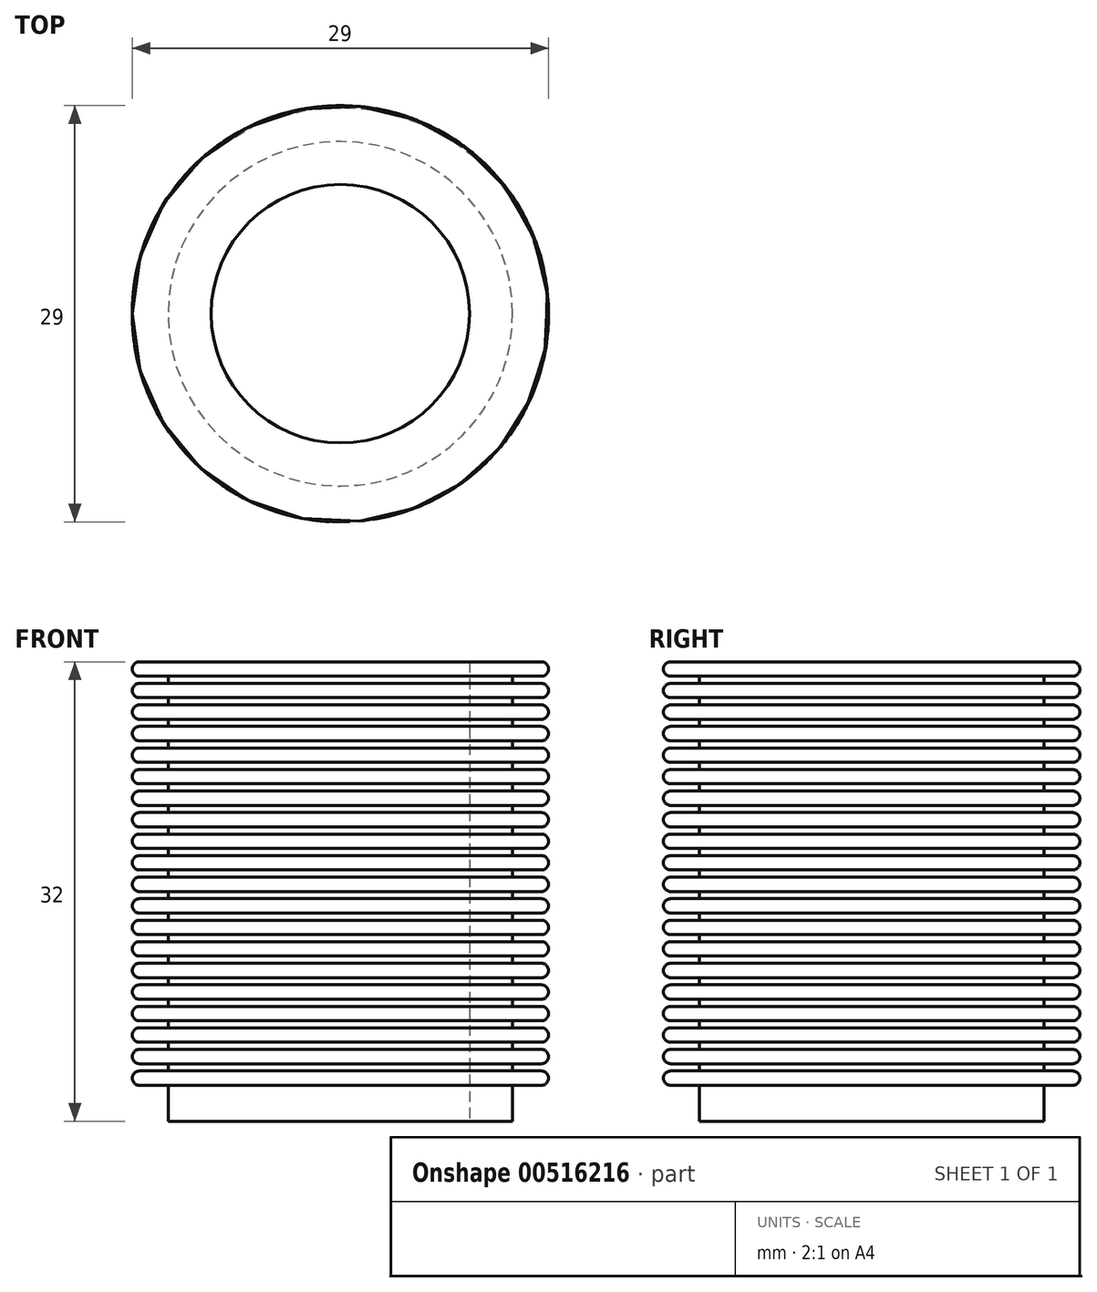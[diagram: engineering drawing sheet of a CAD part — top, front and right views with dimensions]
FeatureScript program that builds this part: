
annotation { "Feature Type Name" : "Feature", "Feature Type Description" : "" }
export const myFeature = defineFeature(function(context is Context, id is Id, definition is map)
    precondition{}
    {
        {
            var Q0;
            Q0=qCreatedBy(makeId("Top.planeOp"),FACE);
            var sketch = newSketch(context, id + "F0", { "sketchPlane" : qUnion([Q0])});
            skCircle(sketch, "E0", {"center": v(0, 0) * mm, "radius": 9 * mm});
            skLineSegment(sketch, "E1.bottom", {"start": v(12.5, 12.5) * mm, "end": v(-12.5, 12.5) * mm});
            skLineSegment(sketch, "E1.top", {"start": v(12.5, -12.5) * mm, "end": v(-12.5, -12.5) * mm});
            skLineSegment(sketch, "E1.left", {"start": v(12.5, 12.5) * mm, "end": v(12.5, -12.5) * mm});
            skLineSegment(sketch, "E1.right", {"start": v(-12.5, 12.5) * mm, "end": v(-12.5, -12.5) * mm});
            skSolve(sketch);
        }
        {
            var Q0;
            Q0=makeQuery(id+"F0.imprint","IMPRINT",FACE,{"disambiguationData":[TD([[makeQuery(id+"F0.imprint","IMPRINT",EDGE,{"derivedFrom":sQuery(id+"F0.wireOp",EDGE,"E0")}),1.0]])]});
            extrude(context, id + "F1", {"entities" : qUnion([Q0]), "depth" : 32 * mm, "offsetDistance" : 25 * mm});
        }
        {
            var Q0;
            Q0=qCreatedBy(makeId("Front.planeOp"),FACE);
            var sketch = newSketch(context, id + "F2", { "sketchPlane" : qUnion([Q0])});
            skLineSegment(sketch, "E2", {"start": v(0, 0) * mm, "end": v(-9, 0) * mm});
            skLineSegment(sketch, "E3.bottom", {"start": v(-9, 0) * mm, "end": v(-12, 0) * mm});
            skLineSegment(sketch, "E3.top", {"start": v(-9, 32) * mm, "end": v(-12, 32) * mm});
            skLineSegment(sketch, "E3.left", {"start": v(-9, 0) * mm, "end": v(-9, 32) * mm});
            skLineSegment(sketch, "E3.right", {"start": v(-12, 0) * mm, "end": v(-12, 32) * mm});
            skLineSegment(sketch, "E4.bottom", {"start": v(-12, 32) * mm, "end": v(-14, 32) * mm});
            skLineSegment(sketch, "E4.top", {"start": v(-12, 31) * mm, "end": v(-14, 31) * mm});
            skLineSegment(sketch, "E4.left", {"start": v(-12, 32) * mm, "end": v(-12, 31) * mm});
            skLineSegment(sketch, "E4.right", {"start": v(-14.5, 31.5) * mm, "end": v(-14.5, 31.5) * mm});
            skPoint(sketch, "E5", {"position": v(-12, 29.83) * mm});
            skLineSegment(sketch, "E6.1.0.0", {"start": v(-14.5, 30) * mm, "end": v(-14.5, 30) * mm});
            skLineSegment(sketch, "E6.1.0.1", {"start": v(-12, 30.5) * mm, "end": v(-14, 30.5) * mm});
            skLineSegment(sketch, "E6.1.0.2", {"start": v(-12, 29.5) * mm, "end": v(-14, 29.5) * mm});
            skLineSegment(sketch, "E6.2.0.0", {"start": v(-14.5, 28.5) * mm, "end": v(-14.5, 28.5) * mm});
            skLineSegment(sketch, "E6.2.0.1", {"start": v(-12, 29) * mm, "end": v(-14, 29) * mm});
            skLineSegment(sketch, "E6.2.0.2", {"start": v(-12, 28) * mm, "end": v(-14, 28) * mm});
            skLineSegment(sketch, "E6.3.0.0", {"start": v(-14.5, 27) * mm, "end": v(-14.5, 27) * mm});
            skLineSegment(sketch, "E6.3.0.1", {"start": v(-12, 27.5) * mm, "end": v(-14, 27.5) * mm});
            skLineSegment(sketch, "E6.3.0.2", {"start": v(-12, 26.5) * mm, "end": v(-14, 26.5) * mm});
            skLineSegment(sketch, "E6.4.0.0", {"start": v(-14.5, 25.5) * mm, "end": v(-14.5, 25.5) * mm});
            skLineSegment(sketch, "E6.4.0.1", {"start": v(-12, 26) * mm, "end": v(-14, 26) * mm});
            skLineSegment(sketch, "E6.4.0.2", {"start": v(-12, 25) * mm, "end": v(-14, 25) * mm});
            skLineSegment(sketch, "E6.5.0.0", {"start": v(-14.5, 24) * mm, "end": v(-14.5, 24) * mm});
            skLineSegment(sketch, "E6.5.0.1", {"start": v(-12, 24.5) * mm, "end": v(-14, 24.5) * mm});
            skLineSegment(sketch, "E6.5.0.2", {"start": v(-12, 23.5) * mm, "end": v(-14, 23.5) * mm});
            skLineSegment(sketch, "E6.6.0.0", {"start": v(-14.5, 22.5) * mm, "end": v(-14.5, 22.5) * mm});
            skLineSegment(sketch, "E6.6.0.1", {"start": v(-12, 23) * mm, "end": v(-14, 23) * mm});
            skLineSegment(sketch, "E6.6.0.2", {"start": v(-12, 22) * mm, "end": v(-14, 22) * mm});
            skLineSegment(sketch, "E6.7.0.0", {"start": v(-14.5, 21) * mm, "end": v(-14.5, 21) * mm});
            skLineSegment(sketch, "E6.7.0.1", {"start": v(-12, 21.5) * mm, "end": v(-14, 21.5) * mm});
            skLineSegment(sketch, "E6.7.0.2", {"start": v(-12, 20.5) * mm, "end": v(-14, 20.5) * mm});
            skLineSegment(sketch, "E6.8.0.0", {"start": v(-14.5, 19.5) * mm, "end": v(-14.5, 19.5) * mm});
            skLineSegment(sketch, "E6.8.0.1", {"start": v(-12, 20) * mm, "end": v(-14, 20) * mm});
            skLineSegment(sketch, "E6.8.0.2", {"start": v(-12, 19) * mm, "end": v(-14, 19) * mm});
            skLineSegment(sketch, "E6.9.0.0", {"start": v(-14.5, 18) * mm, "end": v(-14.5, 18) * mm});
            skLineSegment(sketch, "E6.9.0.1", {"start": v(-12, 18.5) * mm, "end": v(-14, 18.5) * mm});
            skLineSegment(sketch, "E6.9.0.2", {"start": v(-12, 17.5) * mm, "end": v(-14, 17.5) * mm});
            skLineSegment(sketch, "E6.10.0.0", {"start": v(-14.5, 16.5) * mm, "end": v(-14.5, 16.5) * mm});
            skLineSegment(sketch, "E6.10.0.1", {"start": v(-12, 17) * mm, "end": v(-14, 17) * mm});
            skLineSegment(sketch, "E6.10.0.2", {"start": v(-12, 16) * mm, "end": v(-14, 16) * mm});
            skLineSegment(sketch, "E6.11.0.0", {"start": v(-14.5, 15) * mm, "end": v(-14.5, 15) * mm});
            skLineSegment(sketch, "E6.11.0.1", {"start": v(-12, 15.5) * mm, "end": v(-14, 15.5) * mm});
            skLineSegment(sketch, "E6.11.0.2", {"start": v(-12, 14.5) * mm, "end": v(-14, 14.5) * mm});
            skLineSegment(sketch, "E6.12.0.0", {"start": v(-14.5, 13.5) * mm, "end": v(-14.5, 13.5) * mm});
            skLineSegment(sketch, "E6.12.0.1", {"start": v(-12, 14) * mm, "end": v(-14, 14) * mm});
            skLineSegment(sketch, "E6.12.0.2", {"start": v(-12, 13) * mm, "end": v(-14, 13) * mm});
            skLineSegment(sketch, "E6.13.0.0", {"start": v(-14.5, 12) * mm, "end": v(-14.5, 12) * mm});
            skLineSegment(sketch, "E6.13.0.1", {"start": v(-12, 12.5) * mm, "end": v(-14, 12.5) * mm});
            skLineSegment(sketch, "E6.13.0.2", {"start": v(-12, 11.5) * mm, "end": v(-14, 11.5) * mm});
            skLineSegment(sketch, "E6.14.0.0", {"start": v(-14.5, 10.5) * mm, "end": v(-14.5, 10.5) * mm});
            skLineSegment(sketch, "E6.14.0.1", {"start": v(-12, 11) * mm, "end": v(-14, 11) * mm});
            skLineSegment(sketch, "E6.14.0.2", {"start": v(-12, 10) * mm, "end": v(-14, 10) * mm});
            skLineSegment(sketch, "E6.15.0.0", {"start": v(-14.5, 9) * mm, "end": v(-14.5, 9) * mm});
            skLineSegment(sketch, "E6.15.0.1", {"start": v(-12, 9.5) * mm, "end": v(-14, 9.5) * mm});
            skLineSegment(sketch, "E6.15.0.2", {"start": v(-12, 8.5) * mm, "end": v(-14, 8.5) * mm});
            skLineSegment(sketch, "E6.16.0.0", {"start": v(-14.5, 7.5) * mm, "end": v(-14.5, 7.5) * mm});
            skLineSegment(sketch, "E6.16.0.1", {"start": v(-12, 8) * mm, "end": v(-14, 8) * mm});
            skLineSegment(sketch, "E6.16.0.2", {"start": v(-12, 7) * mm, "end": v(-14, 7) * mm});
            skLineSegment(sketch, "E6.17.0.0", {"start": v(-14.5, 6) * mm, "end": v(-14.5, 6) * mm});
            skLineSegment(sketch, "E6.17.0.1", {"start": v(-12, 6.5) * mm, "end": v(-14, 6.5) * mm});
            skLineSegment(sketch, "E6.17.0.2", {"start": v(-12, 5.5) * mm, "end": v(-14, 5.5) * mm});
            skLineSegment(sketch, "E6.18.0.0", {"start": v(-14.5, 4.5) * mm, "end": v(-14.5, 4.5) * mm});
            skLineSegment(sketch, "E6.18.0.1", {"start": v(-12, 5) * mm, "end": v(-14, 5) * mm});
            skLineSegment(sketch, "E6.18.0.2", {"start": v(-12, 4) * mm, "end": v(-14, 4) * mm});
            skLineSegment(sketch, "E6.19.0.0", {"start": v(-14.5, 3) * mm, "end": v(-14.5, 3) * mm});
            skLineSegment(sketch, "E6.19.0.1", {"start": v(-12, 3.5) * mm, "end": v(-14, 3.5) * mm});
            skLineSegment(sketch, "E6.19.0.2", {"start": v(-12, 2.5) * mm, "end": v(-14, 2.5) * mm});
            skLineSegment(sketch, "E6.direction1", {"start": v(-12, 31) * mm, "end": v(-12, 29.5) * mm, "construction": true});
            skPoint(sketch, "E7.visualSharp", {"position": v(-14.5, 32) * mm});
            skArc(sketch, "E7.filletArc", {"start": v(-14, 32) * mm, "mid": v(-14.35, 31.85) * mm, "end": v(-14.5, 31.5) * mm});
            skPoint(sketch, "E8.visualSharp", {"position": v(-14.5, 31) * mm});
            skArc(sketch, "E8.filletArc", {"start": v(-14.5, 31.5) * mm, "mid": v(-14.35, 31.15) * mm, "end": v(-14, 31) * mm});
            skPoint(sketch, "E9.visualSharp", {"position": v(-14.5, 30.5) * mm});
            skArc(sketch, "E9.filletArc", {"start": v(-14, 30.5) * mm, "mid": v(-14.35, 30.35) * mm, "end": v(-14.5, 30) * mm});
            skPoint(sketch, "E10.visualSharp", {"position": v(-14.5, 29.5) * mm});
            skArc(sketch, "E10.filletArc", {"start": v(-14.5, 30) * mm, "mid": v(-14.35, 29.65) * mm, "end": v(-14, 29.5) * mm});
            skPoint(sketch, "E11.visualSharp", {"position": v(-14.5, 29) * mm});
            skArc(sketch, "E11.filletArc", {"start": v(-14, 29) * mm, "mid": v(-14.35, 28.85) * mm, "end": v(-14.5, 28.5) * mm});
            skPoint(sketch, "E12.visualSharp", {"position": v(-14.5, 28) * mm});
            skArc(sketch, "E12.filletArc", {"start": v(-14.5, 28.5) * mm, "mid": v(-14.35, 28.15) * mm, "end": v(-14, 28) * mm});
            skPoint(sketch, "E13.visualSharp", {"position": v(-14.5, 2.5) * mm});
            skArc(sketch, "E13.filletArc", {"start": v(-14.5, 3) * mm, "mid": v(-14.35, 2.65) * mm, "end": v(-14, 2.5) * mm});
            skPoint(sketch, "E14.visualSharp", {"position": v(-14.5, 5) * mm});
            skArc(sketch, "E14.filletArc", {"start": v(-14, 5) * mm, "mid": v(-14.35, 4.85) * mm, "end": v(-14.5, 4.5) * mm});
            skPoint(sketch, "E15.visualSharp", {"position": v(-14.5, 4) * mm});
            skArc(sketch, "E15.filletArc", {"start": v(-14.5, 4.5) * mm, "mid": v(-14.35, 4.15) * mm, "end": v(-14, 4) * mm});
            skPoint(sketch, "E16.visualSharp", {"position": v(-14.5, 3.5) * mm});
            skArc(sketch, "E16.filletArc", {"start": v(-14, 3.5) * mm, "mid": v(-14.35, 3.35) * mm, "end": v(-14.5, 3) * mm});
            skPoint(sketch, "E17.visualSharp", {"position": v(-14.5, 5.5) * mm});
            skArc(sketch, "E17.filletArc", {"start": v(-14.5, 6) * mm, "mid": v(-14.35, 5.65) * mm, "end": v(-14, 5.5) * mm});
            skPoint(sketch, "E18.visualSharp", {"position": v(-14.5, 8) * mm});
            skArc(sketch, "E18.filletArc", {"start": v(-14, 8) * mm, "mid": v(-14.35, 7.85) * mm, "end": v(-14.5, 7.5) * mm});
            skPoint(sketch, "E19.visualSharp", {"position": v(-14.5, 7) * mm});
            skArc(sketch, "E19.filletArc", {"start": v(-14.5, 7.5) * mm, "mid": v(-14.35, 7.15) * mm, "end": v(-14, 7) * mm});
            skPoint(sketch, "E20.visualSharp", {"position": v(-14.5, 9.5) * mm});
            skArc(sketch, "E20.filletArc", {"start": v(-14, 9.5) * mm, "mid": v(-14.35, 9.35) * mm, "end": v(-14.5, 9) * mm});
            skPoint(sketch, "E21.visualSharp", {"position": v(-14.5, 11) * mm});
            skArc(sketch, "E21.filletArc", {"start": v(-14, 11) * mm, "mid": v(-14.35, 10.85) * mm, "end": v(-14.5, 10.5) * mm});
            skPoint(sketch, "E22.visualSharp", {"position": v(-14.5, 10) * mm});
            skArc(sketch, "E22.filletArc", {"start": v(-14.5, 10.5) * mm, "mid": v(-14.35, 10.15) * mm, "end": v(-14, 10) * mm});
            skPoint(sketch, "E23.visualSharp", {"position": v(-14.5, 11.5) * mm});
            skArc(sketch, "E23.filletArc", {"start": v(-14.5, 12) * mm, "mid": v(-14.35, 11.65) * mm, "end": v(-14, 11.5) * mm});
            skPoint(sketch, "E24.visualSharp", {"position": v(-14.5, 12.5) * mm});
            skArc(sketch, "E24.filletArc", {"start": v(-14, 12.5) * mm, "mid": v(-14.35, 12.35) * mm, "end": v(-14.5, 12) * mm});
            skPoint(sketch, "E25.visualSharp", {"position": v(-14.5, 13) * mm});
            skArc(sketch, "E25.filletArc", {"start": v(-14.5, 13.5) * mm, "mid": v(-14.35, 13.15) * mm, "end": v(-14, 13) * mm});
            skPoint(sketch, "E26.visualSharp", {"position": v(-14.5, 14) * mm});
            skArc(sketch, "E26.filletArc", {"start": v(-14, 14) * mm, "mid": v(-14.35, 13.85) * mm, "end": v(-14.5, 13.5) * mm});
            skPoint(sketch, "E27.visualSharp", {"position": v(-14.5, 14.5) * mm});
            skArc(sketch, "E27.filletArc", {"start": v(-14.5, 15) * mm, "mid": v(-14.35, 14.65) * mm, "end": v(-14, 14.5) * mm});
            skPoint(sketch, "E28.visualSharp", {"position": v(-14.5, 16) * mm});
            skArc(sketch, "E28.filletArc", {"start": v(-14.5, 16.5) * mm, "mid": v(-14.35, 16.15) * mm, "end": v(-14, 16) * mm});
            skPoint(sketch, "E29.visualSharp", {"position": v(-14.5, 15.5) * mm});
            skArc(sketch, "E29.filletArc", {"start": v(-14, 15.5) * mm, "mid": v(-14.35, 15.35) * mm, "end": v(-14.5, 15) * mm});
            skPoint(sketch, "E30.visualSharp", {"position": v(-14.5, 17) * mm});
            skArc(sketch, "E30.filletArc", {"start": v(-14, 17) * mm, "mid": v(-14.35, 16.85) * mm, "end": v(-14.5, 16.5) * mm});
            skPoint(sketch, "E31.visualSharp", {"position": v(-14.5, 18.5) * mm});
            skArc(sketch, "E31.filletArc", {"start": v(-14, 18.5) * mm, "mid": v(-14.35, 18.35) * mm, "end": v(-14.5, 18) * mm});
            skPoint(sketch, "E32.visualSharp", {"position": v(-14.5, 20) * mm});
            skArc(sketch, "E32.filletArc", {"start": v(-14, 20) * mm, "mid": v(-14.35, 19.85) * mm, "end": v(-14.5, 19.5) * mm});
            skPoint(sketch, "E33.visualSharp", {"position": v(-14.5, 21.5) * mm});
            skArc(sketch, "E33.filletArc", {"start": v(-14, 21.5) * mm, "mid": v(-14.35, 21.35) * mm, "end": v(-14.5, 21) * mm});
            skPoint(sketch, "E34.visualSharp", {"position": v(-14.5, 23) * mm});
            skArc(sketch, "E34.filletArc", {"start": v(-14, 23) * mm, "mid": v(-14.35, 22.85) * mm, "end": v(-14.5, 22.5) * mm});
            skPoint(sketch, "E35.visualSharp", {"position": v(-14.5, 24.5) * mm});
            skArc(sketch, "E35.filletArc", {"start": v(-14, 24.5) * mm, "mid": v(-14.35, 24.35) * mm, "end": v(-14.5, 24) * mm});
            skPoint(sketch, "E36.visualSharp", {"position": v(-14.5, 26) * mm});
            skArc(sketch, "E36.filletArc", {"start": v(-14, 26) * mm, "mid": v(-14.35, 25.85) * mm, "end": v(-14.5, 25.5) * mm});
            skPoint(sketch, "E37.visualSharp", {"position": v(-14.5, 27.5) * mm});
            skArc(sketch, "E37.filletArc", {"start": v(-14, 27.5) * mm, "mid": v(-14.35, 27.35) * mm, "end": v(-14.5, 27) * mm});
            skPoint(sketch, "E38.visualSharp", {"position": v(-14.5, 26.5) * mm});
            skArc(sketch, "E38.filletArc", {"start": v(-14.5, 27) * mm, "mid": v(-14.35, 26.65) * mm, "end": v(-14, 26.5) * mm});
            skPoint(sketch, "E39.visualSharp", {"position": v(-14.5, 25) * mm});
            skArc(sketch, "E39.filletArc", {"start": v(-14.5, 25.5) * mm, "mid": v(-14.35, 25.15) * mm, "end": v(-14, 25) * mm});
            skPoint(sketch, "E40.visualSharp", {"position": v(-14.5, 19) * mm});
            skArc(sketch, "E40.filletArc", {"start": v(-14.5, 19.5) * mm, "mid": v(-14.35, 19.15) * mm, "end": v(-14, 19) * mm});
            skPoint(sketch, "E41.visualSharp", {"position": v(-14.5, 17.5) * mm});
            skArc(sketch, "E41.filletArc", {"start": v(-14.5, 18) * mm, "mid": v(-14.35, 17.65) * mm, "end": v(-14, 17.5) * mm});
            skPoint(sketch, "E42.visualSharp", {"position": v(-14.5, 20.5) * mm});
            skArc(sketch, "E42.filletArc", {"start": v(-14.5, 21) * mm, "mid": v(-14.35, 20.65) * mm, "end": v(-14, 20.5) * mm});
            skPoint(sketch, "E43.visualSharp", {"position": v(-14.5, 22) * mm});
            skArc(sketch, "E43.filletArc", {"start": v(-14.5, 22.5) * mm, "mid": v(-14.35, 22.15) * mm, "end": v(-14, 22) * mm});
            skPoint(sketch, "E44.visualSharp", {"position": v(-14.5, 23.5) * mm});
            skArc(sketch, "E44.filletArc", {"start": v(-14.5, 24) * mm, "mid": v(-14.35, 23.65) * mm, "end": v(-14, 23.5) * mm});
            skPoint(sketch, "E45.visualSharp", {"position": v(-14.5, 6.5) * mm});
            skArc(sketch, "E45.filletArc", {"start": v(-14, 6.5) * mm, "mid": v(-14.35, 6.35) * mm, "end": v(-14.5, 6) * mm});
            skPoint(sketch, "E46.visualSharp", {"position": v(-14.5, 8.5) * mm});
            skArc(sketch, "E46.filletArc", {"start": v(-14.5, 9) * mm, "mid": v(-14.35, 8.65) * mm, "end": v(-14, 8.5) * mm});
            skLineSegment(sketch, "E47", {"start": v(0, 0) * mm, "end": v(0, 33.63) * mm});
            skSolve(sketch);
        }
        {
            var Q0;
            {var subQ1=sQuery(id+"F2.wireOp",EDGE,"E6.1.0.1");Q0=makeQuery(id+"F2.imprint","IMPRINT",FACE,{"disambiguationData":[TD([[makeQuery(id+"F2.imprint","IMPRINT",EDGE,{"derivedFrom":subQ1}),1.0]])]});}
            var Q1;
            Q1=makeQuery(id+"F2.imprint","IMPRINT",FACE,{"disambiguationData":[TD([[makeQuery(id+"F2.imprint","IMPRINT",EDGE,{"derivedFrom":sQuery(id+"F2.wireOp",EDGE,"E4.bottom")}),1.0]])]});
            var Q2;
            {var subQ0=sQuery(id+"F2.wireOp",EDGE,"E6.2.0.1");Q2=makeQuery(id+"F2.imprint","IMPRINT",FACE,{"disambiguationData":[TD([[makeQuery(id+"F2.imprint","IMPRINT",EDGE,{"derivedFrom":subQ0}),1.0]])]});}
            var Q3;
            {var subQ0=sQuery(id+"F2.wireOp",EDGE,"E6.3.0.1");Q3=makeQuery(id+"F2.imprint","IMPRINT",FACE,{"disambiguationData":[TD([[makeQuery(id+"F2.imprint","IMPRINT",EDGE,{"derivedFrom":subQ0}),1.0]])]});}
            var Q4;
            {var subQ1=sQuery(id+"F2.wireOp",EDGE,"E6.4.0.1");Q4=makeQuery(id+"F2.imprint","IMPRINT",FACE,{"disambiguationData":[TD([[makeQuery(id+"F2.imprint","IMPRINT",EDGE,{"derivedFrom":subQ1}),1.0]])]});}
            var Q5;
            {var subQ1=sQuery(id+"F2.wireOp",EDGE,"E6.5.0.1");Q5=makeQuery(id+"F2.imprint","IMPRINT",FACE,{"disambiguationData":[TD([[makeQuery(id+"F2.imprint","IMPRINT",EDGE,{"derivedFrom":subQ1}),1.0]])]});}
            var Q6;
            {var subQ1=sQuery(id+"F2.wireOp",EDGE,"E6.6.0.1");Q6=makeQuery(id+"F2.imprint","IMPRINT",FACE,{"disambiguationData":[TD([[makeQuery(id+"F2.imprint","IMPRINT",EDGE,{"derivedFrom":subQ1}),1.0]])]});}
            var Q7;
            {var subQ0=sQuery(id+"F2.wireOp",EDGE,"E6.7.0.1");Q7=makeQuery(id+"F2.imprint","IMPRINT",FACE,{"disambiguationData":[TD([[makeQuery(id+"F2.imprint","IMPRINT",EDGE,{"derivedFrom":subQ0}),1.0]])]});}
            var Q8;
            {var subQ1=sQuery(id+"F2.wireOp",EDGE,"E6.8.0.1");Q8=makeQuery(id+"F2.imprint","IMPRINT",FACE,{"disambiguationData":[TD([[makeQuery(id+"F2.imprint","IMPRINT",EDGE,{"derivedFrom":subQ1}),1.0]])]});}
            var Q9;
            {var subQ1=sQuery(id+"F2.wireOp",EDGE,"E6.9.0.1");Q9=makeQuery(id+"F2.imprint","IMPRINT",FACE,{"disambiguationData":[TD([[makeQuery(id+"F2.imprint","IMPRINT",EDGE,{"derivedFrom":subQ1}),1.0]])]});}
            var Q10;
            {var subQ1=sQuery(id+"F2.wireOp",EDGE,"E6.10.0.1");Q10=makeQuery(id+"F2.imprint","IMPRINT",FACE,{"disambiguationData":[TD([[makeQuery(id+"F2.imprint","IMPRINT",EDGE,{"derivedFrom":subQ1}),1.0]])]});}
            var Q11;
            {var subQ1=sQuery(id+"F2.wireOp",EDGE,"E6.11.0.1");Q11=makeQuery(id+"F2.imprint","IMPRINT",FACE,{"disambiguationData":[TD([[makeQuery(id+"F2.imprint","IMPRINT",EDGE,{"derivedFrom":subQ1}),1.0]])]});}
            var Q12;
            {var subQ1=sQuery(id+"F2.wireOp",EDGE,"E6.12.0.1");Q12=makeQuery(id+"F2.imprint","IMPRINT",FACE,{"disambiguationData":[TD([[makeQuery(id+"F2.imprint","IMPRINT",EDGE,{"derivedFrom":subQ1}),1.0]])]});}
            var Q13;
            {var subQ1=sQuery(id+"F2.wireOp",EDGE,"E6.13.0.1");Q13=makeQuery(id+"F2.imprint","IMPRINT",FACE,{"disambiguationData":[TD([[makeQuery(id+"F2.imprint","IMPRINT",EDGE,{"derivedFrom":subQ1}),1.0]])]});}
            var Q14;
            {var subQ1=sQuery(id+"F2.wireOp",EDGE,"E6.14.0.1");Q14=makeQuery(id+"F2.imprint","IMPRINT",FACE,{"disambiguationData":[TD([[makeQuery(id+"F2.imprint","IMPRINT",EDGE,{"derivedFrom":subQ1}),1.0]])]});}
            var Q15;
            {var subQ1=sQuery(id+"F2.wireOp",EDGE,"E6.15.0.1");Q15=makeQuery(id+"F2.imprint","IMPRINT",FACE,{"disambiguationData":[TD([[makeQuery(id+"F2.imprint","IMPRINT",EDGE,{"derivedFrom":subQ1}),1.0]])]});}
            var Q16;
            {var subQ1=sQuery(id+"F2.wireOp",EDGE,"E6.16.0.1");Q16=makeQuery(id+"F2.imprint","IMPRINT",FACE,{"disambiguationData":[TD([[makeQuery(id+"F2.imprint","IMPRINT",EDGE,{"derivedFrom":subQ1}),1.0]])]});}
            var Q17;
            {var subQ0=sQuery(id+"F2.wireOp",EDGE,"E6.17.0.1");Q17=makeQuery(id+"F2.imprint","IMPRINT",FACE,{"disambiguationData":[TD([[makeQuery(id+"F2.imprint","IMPRINT",EDGE,{"derivedFrom":subQ0}),1.0]])]});}
            var Q18;
            {var subQ0=sQuery(id+"F2.wireOp",EDGE,"E6.18.0.1");Q18=makeQuery(id+"F2.imprint","IMPRINT",FACE,{"disambiguationData":[TD([[makeQuery(id+"F2.imprint","IMPRINT",EDGE,{"derivedFrom":subQ0}),1.0]])]});}
            var Q19;
            {var subQ1=sQuery(id+"F2.wireOp",EDGE,"E6.19.0.1");Q19=makeQuery(id+"F2.imprint","IMPRINT",FACE,{"disambiguationData":[TD([[makeQuery(id+"F2.imprint","IMPRINT",EDGE,{"derivedFrom":subQ1}),1.0]])]});}
            var Q20;
            {var subQ14=sQuery(id+"F2.wireOp",EDGE,"E3.bottom");Q20=makeQuery(id+"F2.imprint","IMPRINT",FACE,{"disambiguationData":[TD([[makeQuery(id+"F2.imprint","IMPRINT",EDGE,{"derivedFrom":subQ14}),-1.0]])]});}
            var Q21;
            Q21=sQuery(id+"F2.wireOp",EDGE,"E47");
            revolve(context, id + "F3", {"operationType" : NewBodyOperationType.ADD, "entities" : qUnion([Q0, Q1, Q2, Q3, Q4, Q5, Q6, Q7, Q8, Q9, Q10, Q11, Q12, Q13, Q14, Q15, Q16, Q17, Q18, Q19, Q20]), "axis" : qUnion([Q21]), "revolveType" : RevolveType.FULL});
        }
        {
            var Q0;
            Q0=makeQuery(id+"F0.imprint","IMPRINT",FACE,{"disambiguationData":[TD([[makeQuery(id+"F0.imprint","IMPRINT",EDGE,{"derivedFrom":sQuery(id+"F0.wireOp",EDGE,"E0")}),1.0]])]});
            extrude(context, id + "F4", {"entities" : qUnion([Q0]), "operationType" : NewBodyOperationType.REMOVE, "depth" : 40 * mm, "offsetDistance" : 25 * mm});
        }
    });
